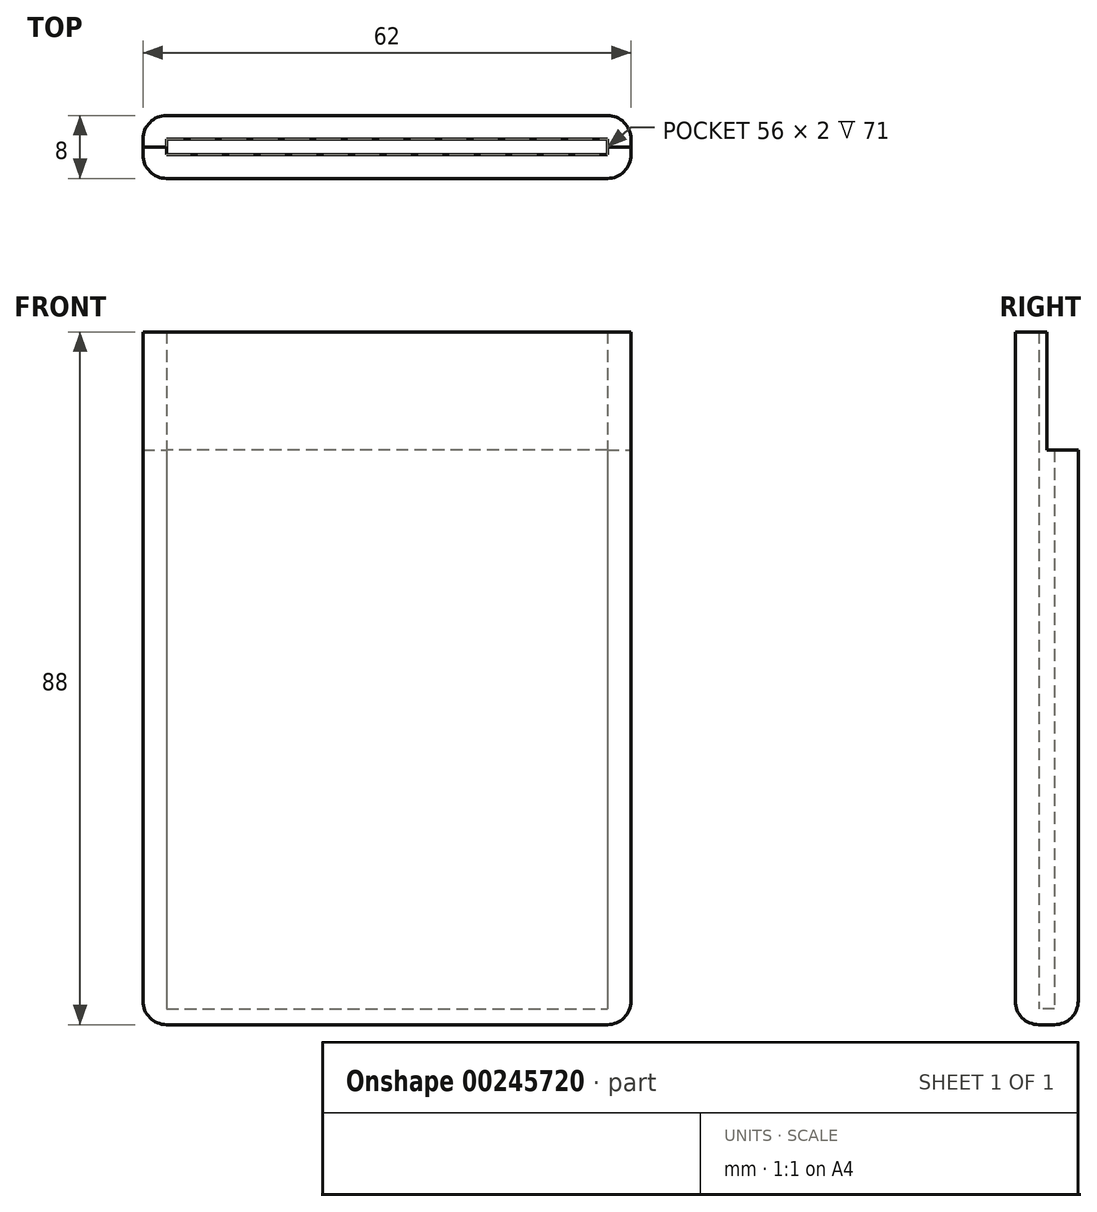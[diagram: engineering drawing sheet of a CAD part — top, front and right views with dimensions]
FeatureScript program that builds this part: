
annotation { "Feature Type Name" : "Feature", "Feature Type Description" : "" }
export const myFeature = defineFeature(function(context is Context, id is Id, definition is map)
    precondition{}
    {
        {
            var Q0;
            Q0=qCreatedBy(makeId("Top.planeOp"),FACE);
            var sketch = newSketch(context, id + "F0", { "sketchPlane" : qUnion([Q0])});
            skLineSegment(sketch, "E0.bottom", {"start": v(-28, 1) * mm, "end": v(28, 1) * mm});
            skLineSegment(sketch, "E0.top", {"start": v(-28, -1) * mm, "end": v(28, -1) * mm});
            skLineSegment(sketch, "E0.left", {"start": v(-28, 1) * mm, "end": v(-28, -1) * mm});
            skLineSegment(sketch, "E0.right", {"start": v(28, 1) * mm, "end": v(28, -1) * mm});
            skLineSegment(sketch, "E1.bottom", {"start": v(-31, 4) * mm, "end": v(31, 4) * mm});
            skLineSegment(sketch, "E1.top", {"start": v(-31, -4) * mm, "end": v(31, -4) * mm});
            skLineSegment(sketch, "E1.left", {"start": v(-31, 4) * mm, "end": v(-31, -4) * mm});
            skLineSegment(sketch, "E1.right", {"start": v(31, 4) * mm, "end": v(31, -4) * mm});
            skSolve(sketch);
        }
        {
            var Q0;
            Q0=makeQuery(id+"F0.imprint","IMPRINT",FACE,{"disambiguationData":[TD([[makeQuery(id+"F0.imprint","IMPRINT",EDGE,{"derivedFrom":sQuery(id+"F0.wireOp",EDGE,"E0.bottom")}),1.0]])]});
            extrude(context, id + "F1", {"entities" : qUnion([Q0]), "depth" : 86 * mm});
        }
        {
            var Q0;
            Q0=qCreatedBy(makeId("Front.planeOp"),FACE);
            var sketch = newSketch(context, id + "F2", { "sketchPlane" : qUnion([Q0])});
            skLineSegment(sketch, "E2.bottom", {"start": v(-31, 86) * mm, "end": v(31, 86) * mm});
            skLineSegment(sketch, "E2.top", {"start": v(-31, 71) * mm, "end": v(31, 71) * mm});
            skLineSegment(sketch, "E2.left", {"start": v(-31, 86) * mm, "end": v(-31, 71) * mm});
            skLineSegment(sketch, "E2.right", {"start": v(31, 86) * mm, "end": v(31, 71) * mm});
            skSolve(sketch);
        }
        {
            var Q0;
            Q0=makeQuery(id+"F2.imprint","IMPRINT",FACE,{"disambiguationData":[TD([[makeQuery(id+"F2.imprint","IMPRINT",EDGE,{"derivedFrom":sQuery(id+"F2.wireOp",EDGE,"E2.bottom")}),-1.0]])]});
            extrude(context, id + "F3", {"entities" : qUnion([Q0]), "operationType" : NewBodyOperationType.REMOVE, "oppositeDirection" : true, "depth" : 5 * mm});
        }
        {
            var Q0;
            Q0=qCreatedBy(makeId("Front.planeOp"),FACE);
            var sketch = newSketch(context, id + "F4", { "sketchPlane" : qUnion([Q0])});
            skLineSegment(sketch, "E3.bottom", {"start": v(31, 0) * mm, "end": v(-31, 0) * mm});
            skLineSegment(sketch, "E3.top", {"start": v(31, -2) * mm, "end": v(-31, -2) * mm});
            skLineSegment(sketch, "E3.left", {"start": v(31, 0) * mm, "end": v(31, -2) * mm});
            skLineSegment(sketch, "E3.right", {"start": v(-31, 0) * mm, "end": v(-31, -2) * mm});
            skSolve(sketch);
        }
        {
            var Q0;
            Q0=makeQuery(id+"F4.imprint","IMPRINT",FACE,{"disambiguationData":[TD([[makeQuery(id+"F4.imprint","IMPRINT",EDGE,{"derivedFrom":sQuery(id+"F4.wireOp",EDGE,"E3.bottom")}),1.0]])]});
            var Q1;
            Q1=sQuery(id+"F4.wireOp",EDGE,"E3.top");
            extrude(context, id + "F5", {"entities" : qUnion([Q0]), "operationType" : NewBodyOperationType.ADD, "surfaceEntities" : qUnion([Q1]), "endBound" : BoundingType.SYMMETRIC, "oppositeDirection" : true, "depth" : 8 * mm});
        }
        {
            var Q0;
            Q0=makeQuery(id+"F5.opExtrude","CAP_EDGE",EDGE,{"disambiguationData":[OSD([sQuery(id+"F4.wireOp",EDGE,"E3.top")])],"isStart":true});
            var Q1;
            Q1=makeQuery(id+"F5.opExtrude","CAP_EDGE",EDGE,{"disambiguationData":[OSD([sQuery(id+"F4.wireOp",EDGE,"E3.top")])],"isStart":false});
            var Q2;
            Q2=makeQuery(id+"F5.opExtrude","SWEPT_EDGE",EDGE,{"disambiguationData":[OSD([sQuery(id+"F4.wireOp",EDGE,"E3.top"),sQuery(id+"F4.wireOp",EDGE,"E3.left")])]});
            var Q3;
            Q3=makeQuery(id+"F5.opExtrude","SWEPT_EDGE",EDGE,{"disambiguationData":[OSD([sQuery(id+"F4.wireOp",EDGE,"E3.top"),sQuery(id+"F4.wireOp",EDGE,"E3.right")])]});
            var Q4;
            Q4=makeQuery(id+"F5.boolean.opBoolean","MERGE",EDGE,{"derivedFrom":[makeQuery(id+"F1.opExtrude","SWEPT_EDGE",EDGE,{"disambiguationData":[OSD([sQuery(id+"F0.wireOp",EDGE,"E1.bottom"),sQuery(id+"F0.wireOp",EDGE,"E1.right")])]}),makeQuery(id+"F5.opExtrude","CAP_EDGE",EDGE,{"disambiguationData":[OSD([sQuery(id+"F4.wireOp",EDGE,"E3.left")])],"isStart":false})]});
            var Q5;
            Q5=makeQuery(id+"F5.boolean.opBoolean","MERGE",EDGE,{"derivedFrom":[makeQuery(id+"F1.opExtrude","SWEPT_EDGE",EDGE,{"disambiguationData":[OSD([sQuery(id+"F0.wireOp",EDGE,"E1.top"),sQuery(id+"F0.wireOp",EDGE,"E1.right")])]}),makeQuery(id+"F5.opExtrude","CAP_EDGE",EDGE,{"disambiguationData":[OSD([sQuery(id+"F4.wireOp",EDGE,"E3.left")])],"isStart":true})]});
            var Q6;
            Q6=makeQuery(id+"F5.boolean.opBoolean","MERGE",EDGE,{"derivedFrom":[makeQuery(id+"F1.opExtrude","SWEPT_EDGE",EDGE,{"disambiguationData":[OSD([sQuery(id+"F0.wireOp",EDGE,"E1.bottom"),sQuery(id+"F0.wireOp",EDGE,"E1.left")])]}),makeQuery(id+"F5.opExtrude","CAP_EDGE",EDGE,{"disambiguationData":[OSD([sQuery(id+"F4.wireOp",EDGE,"E3.right")])],"isStart":false})]});
            var Q7;
            Q7=makeQuery(id+"F5.boolean.opBoolean","MERGE",EDGE,{"derivedFrom":[makeQuery(id+"F1.opExtrude","SWEPT_EDGE",EDGE,{"disambiguationData":[OSD([sQuery(id+"F0.wireOp",EDGE,"E1.top"),sQuery(id+"F0.wireOp",EDGE,"E1.left")])]}),makeQuery(id+"F5.opExtrude","CAP_EDGE",EDGE,{"disambiguationData":[OSD([sQuery(id+"F4.wireOp",EDGE,"E3.right")])],"isStart":true})]});
            fillet(context, id + "F6", {"entities" : qUnion([Q0, Q1, Q2, Q3, Q4, Q5, Q6, Q7]), "radius" : 3 * mm, "tangentPropagation" : true, "allowEdgeOverflow" : false});
        }
    });
